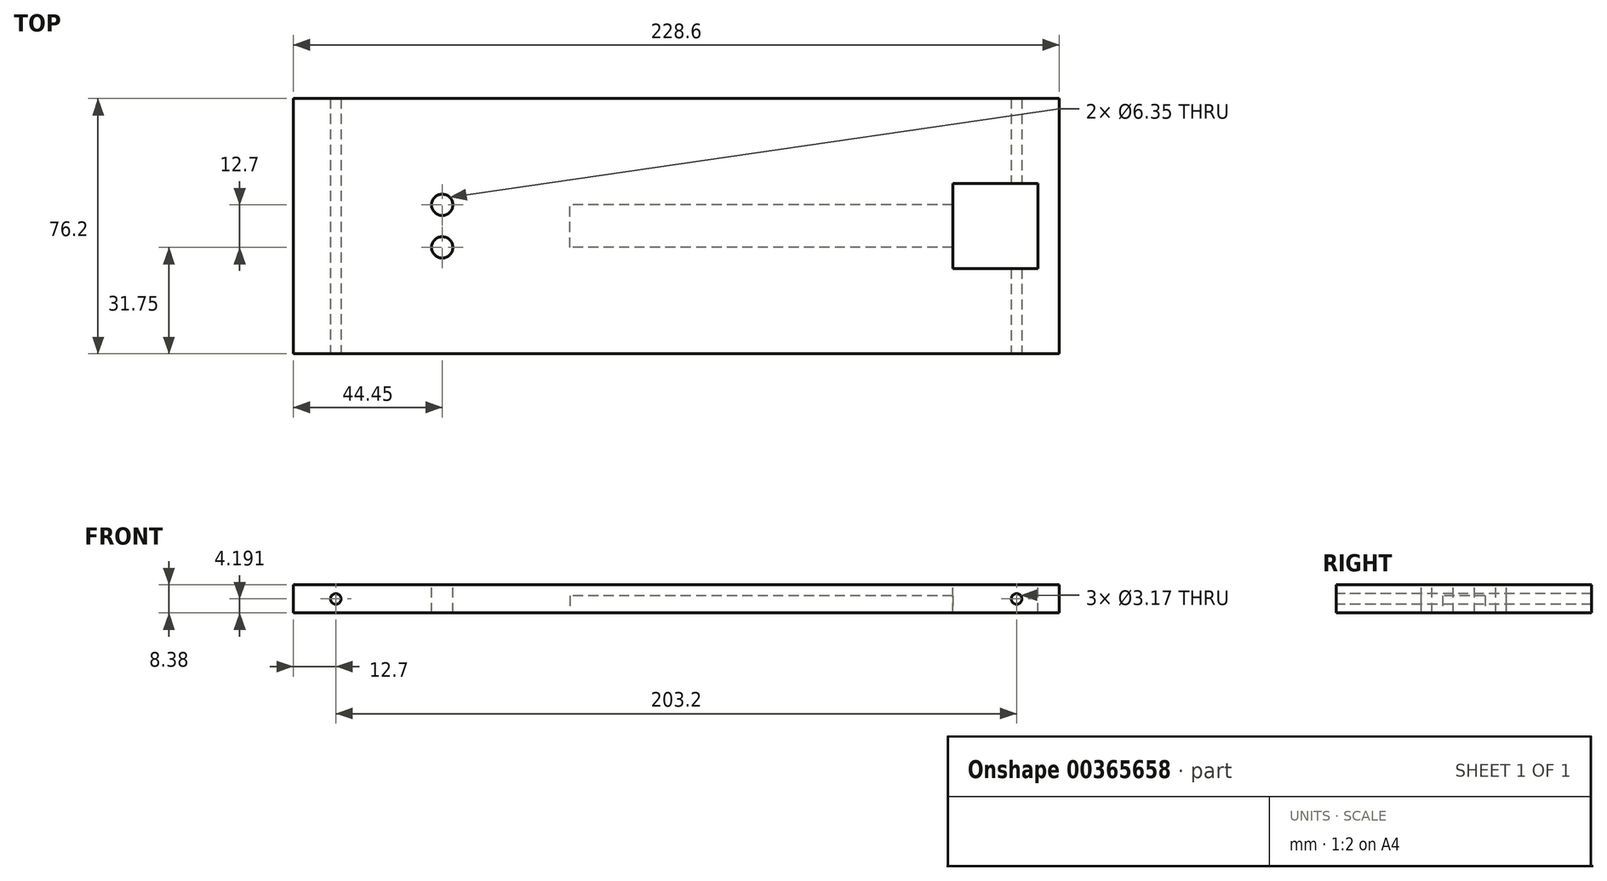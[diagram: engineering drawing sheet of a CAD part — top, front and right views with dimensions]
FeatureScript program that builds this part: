
annotation { "Feature Type Name" : "Feature", "Feature Type Description" : "" }
export const myFeature = defineFeature(function(context is Context, id is Id, definition is map)
    precondition{}
    {
        {
            var Q0;
            Q0=qCreatedBy(makeId("Front.planeOp"),FACE);
            var sketch = newSketch(context, id + "F0", { "sketchPlane" : qUnion([Q0])});
            skLineSegment(sketch, "E0.bottom", {"start": v(0, 0) * mm, "end": v(228.6, 0) * mm});
            skLineSegment(sketch, "E0.top", {"start": v(0, 8.38) * mm, "end": v(228.6, 8.38) * mm});
            skLineSegment(sketch, "E0.left", {"start": v(0, 0) * mm, "end": v(0, 8.38) * mm});
            skLineSegment(sketch, "E0.right", {"start": v(228.6, 0) * mm, "end": v(228.6, 8.38) * mm});
            skSolve(sketch);
        }
        {
            var Q0;
            Q0 = qSketchRegion(id + "F0", true);
            extrude(context, id + "F1", {"entities" : qUnion([Q0]), "depth" : 76.2 * mm});
        }
        {
            var Q0;
            Q0=makeQuery(id+"F1.opExtrude","CAP_FACE",FACE,{"disambiguationData":[OSD([sQuery(id+"F0.wireOp",EDGE,"E0.bottom"),sQuery(id+"F0.wireOp",EDGE,"E0.top"),sQuery(id+"F0.wireOp",EDGE,"E0.left"),sQuery(id+"F0.wireOp",EDGE,"E0.right")])],"isStart":false});
            var sketch = newSketch(context, id + "F2", { "sketchPlane" : qUnion([Q0])});
            skCircle(sketch, "E1", {"center": v(12.7, 4.2) * mm, "radius": 1.59 * mm});
            skCircle(sketch, "E2", {"center": v(215.9, 4.2) * mm, "radius": 1.59 * mm});
            skSolve(sketch);
        }
        {
            var Q0;
            Q0 = qSketchRegion(id + "F2", true);
            extrude(context, id + "F3", {"entities" : qUnion([Q0]), "operationType" : NewBodyOperationType.REMOVE, "endBound" : BoundingType.THROUGH_ALL, "oppositeDirection" : true, "depth" : 25.4 * mm});
        }
        {
            var Q0;
            Q0=makeQuery(id+"F1.opExtrude","SWEPT_FACE",FACE,{"disambiguationData":[OSD([sQuery(id+"F0.wireOp",EDGE,"E0.top")])]});
            var sketch = newSketch(context, id + "F4", { "sketchPlane" : qUnion([Q0])});
            skLineSegment(sketch, "E3.bottom", {"start": v(196.85, -25.4) * mm, "end": v(222.25, -25.4) * mm});
            skLineSegment(sketch, "E3.top", {"start": v(196.85, -50.8) * mm, "end": v(222.25, -50.8) * mm});
            skLineSegment(sketch, "E3.left", {"start": v(196.85, -25.4) * mm, "end": v(196.85, -50.8) * mm});
            skLineSegment(sketch, "E3.right", {"start": v(222.25, -25.4) * mm, "end": v(222.25, -50.8) * mm});
            skCircle(sketch, "E4", {"center": v(44.45, -31.75) * mm, "radius": 3.18 * mm});
            skCircle(sketch, "E5", {"center": v(44.45, -44.45) * mm, "radius": 3.18 * mm});
            skSolve(sketch);
        }
        {
            var Q0;
            Q0 = qSketchRegion(id + "F4", true);
            extrude(context, id + "F5", {"entities" : qUnion([Q0]), "operationType" : NewBodyOperationType.REMOVE, "endBound" : BoundingType.THROUGH_ALL, "oppositeDirection" : true, "depth" : 25.4 * mm});
        }
        {
            var Q0;
            Q0=makeQuery(id+"F1.opExtrude","SWEPT_FACE",FACE,{"disambiguationData":[OSD([sQuery(id+"F0.wireOp",EDGE,"E0.bottom")])]});
            var sketch = newSketch(context, id + "F6", { "sketchPlane" : qUnion([Q0])});
            skLineSegment(sketch, "E6.bottom", {"start": v(196.85, 44.45) * mm, "end": v(82.55, 44.45) * mm});
            skLineSegment(sketch, "E6.top", {"start": v(196.85, 31.75) * mm, "end": v(82.55, 31.75) * mm});
            skLineSegment(sketch, "E6.left", {"start": v(196.85, 44.45) * mm, "end": v(196.85, 31.75) * mm});
            skLineSegment(sketch, "E6.right", {"start": v(82.55, 44.45) * mm, "end": v(82.55, 31.75) * mm});
            skSolve(sketch);
        }
        {
            var Q0;
            Q0 = qSketchRegion(id + "F6", true);
            extrude(context, id + "F7", {"entities" : qUnion([Q0]), "operationType" : NewBodyOperationType.REMOVE, "oppositeDirection" : true, "depth" : 5.08 * mm});
        }
    });
